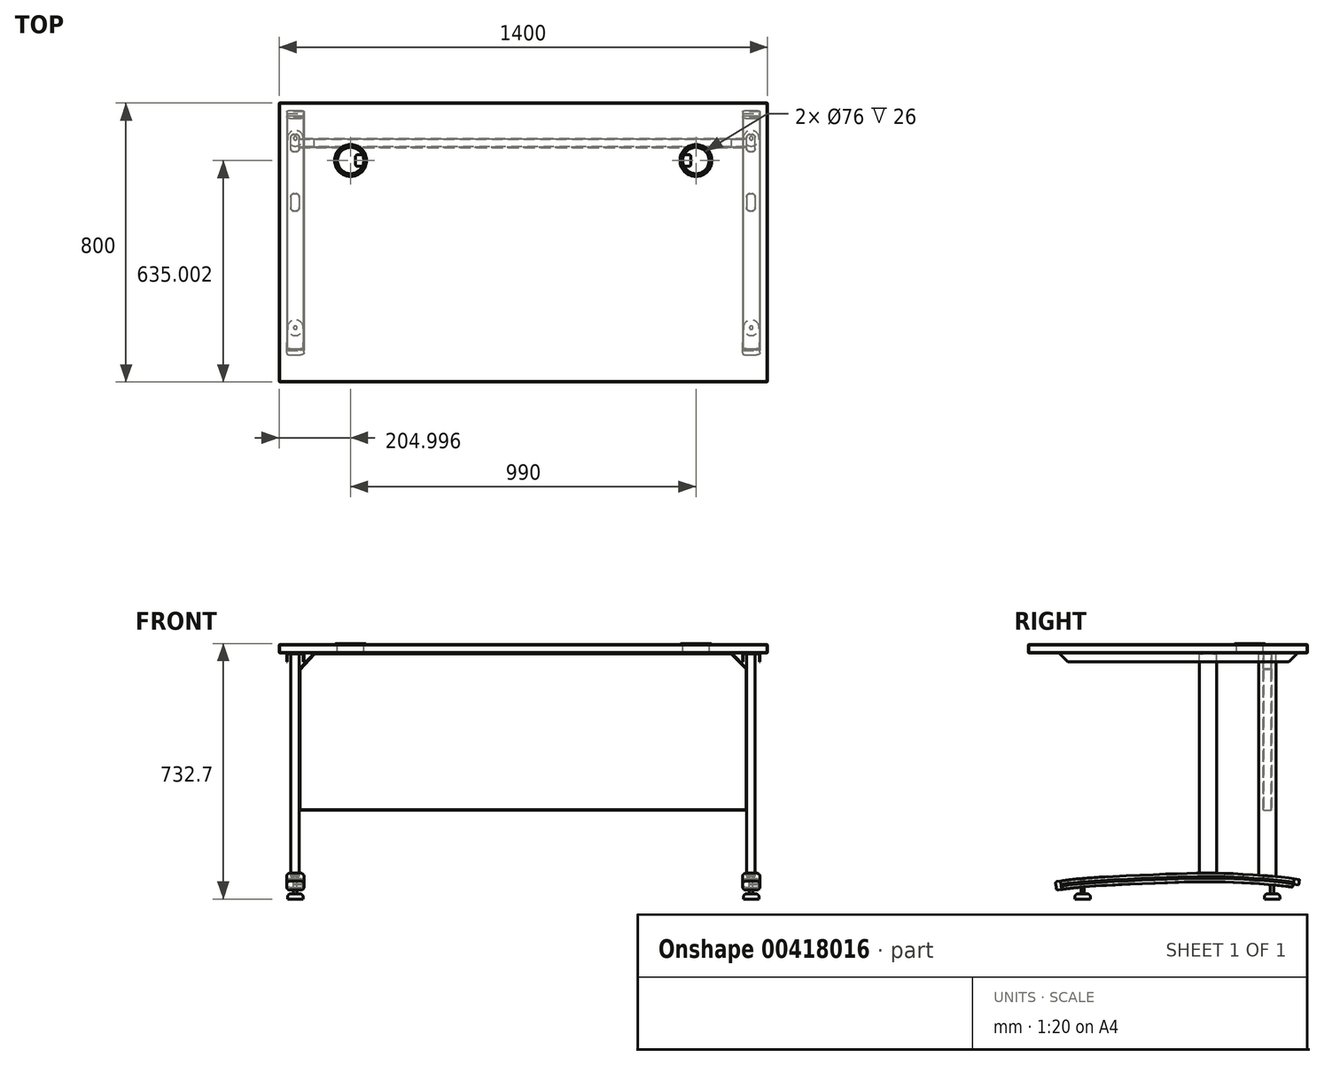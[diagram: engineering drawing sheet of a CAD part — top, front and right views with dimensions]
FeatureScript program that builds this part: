
annotation { "Feature Type Name" : "Feature", "Feature Type Description" : "" }
export const myFeature = defineFeature(function(context is Context, id is Id, definition is map)
    precondition{}
    {
        {
            var Q0;
            Q0=qCreatedBy(makeId("Top.planeOp"),FACE);
            var sketch = newSketch(context, id + "F0", { "sketchPlane" : qUnion([Q0])});
            skLineSegment(sketch, "E0.bottom", {"start": v(-639.54, 396.7) * mm, "end": v(760.46, 396.7) * mm});
            skLineSegment(sketch, "E0.top", {"start": v(-639.54, -403.3) * mm, "end": v(760.46, -403.3) * mm});
            skLineSegment(sketch, "E0.left", {"start": v(-639.54, 396.7) * mm, "end": v(-639.54, -403.3) * mm});
            skLineSegment(sketch, "E0.right", {"start": v(760.46, 396.7) * mm, "end": v(760.46, -403.3) * mm});
            skCircle(sketch, "E1", {"center": v(555.46, 231.7) * mm, "radius": 39 * mm});
            skCircle(sketch, "E2", {"center": v(-434.54, 231.7) * mm, "radius": 39 * mm});
            skSolve(sketch);
        }
        {
            var Q0;
            Q0=makeQuery(id+"F0.imprint","IMPRINT",FACE,{"disambiguationData":[TD([[makeQuery(id+"F0.imprint","IMPRINT",EDGE,{"derivedFrom":sQuery(id+"F0.wireOp",EDGE,"E0.bottom")}),-1.0]])]});
            extrude(context, id + "F1", {"entities" : qUnion([Q0]), "depth" : 25 * mm});
        }
        {
            var Q0;
            Q0=makeQuery(id+"F1.opExtrude","CAP_FACE",FACE,{"disambiguationData":[OSD([sQuery(id+"F0.wireOp",EDGE,"E0.bottom"),sQuery(id+"F0.wireOp",EDGE,"E0.top"),sQuery(id+"F0.wireOp",EDGE,"E0.left"),sQuery(id+"F0.wireOp",EDGE,"E0.right"),sQuery(id+"F0.wireOp",EDGE,"E1"),sQuery(id+"F0.wireOp",EDGE,"E2")])],"isStart":false});
            var sketch = newSketch(context, id + "F2", { "sketchPlane" : qUnion([Q0])});
            skCircle(sketch, "E3", {"center": v(555.46, 231.7) * mm, "radius": 45 * mm});
            skCircle(sketch, "E4", {"center": v(-434.54, 231.7) * mm, "radius": 45 * mm});
            skCircle(sketch, "E5", {"center": v(555.46, 231.7) * mm, "radius": 38 * mm});
            skCircle(sketch, "E6", {"center": v(555.46, 231.7) * mm, "radius": 39 * mm});
            skCircle(sketch, "E7", {"center": v(-434.54, 231.7) * mm, "radius": 39 * mm});
            skCircle(sketch, "E8", {"center": v(-434.54, 231.7) * mm, "radius": 38 * mm});
            skSolve(sketch);
        }
        {
            var Q0;
            Q0=makeQuery(id+"F2.imprint","IMPRINT",FACE,{"disambiguationData":[TD([[makeQuery(id+"F2.imprint","IMPRINT",EDGE,{"derivedFrom":sQuery(id+"F2.wireOp",EDGE,"E7")}),1.0]])]});
            var Q1;
            Q1=makeQuery(id+"F2.imprint","IMPRINT",FACE,{"disambiguationData":[TD([[makeQuery(id+"F2.imprint","IMPRINT",EDGE,{"derivedFrom":sQuery(id+"F2.wireOp",EDGE,"E5")}),-1.0]])]});
            extrude(context, id + "F3", {"entities" : qUnion([Q0, Q1]), "oppositeDirection" : true, "depth" : 25 * mm});
        }
        {
            var Q0;
            Q0=makeQuery(id+"F2.imprint","IMPRINT",FACE,{"disambiguationData":[TD([[makeQuery(id+"F2.imprint","IMPRINT",EDGE,{"derivedFrom":sQuery(id+"F2.wireOp",EDGE,"E4")}),1.0]])]});
            var Q1;
            Q1=makeQuery(id+"F2.imprint","IMPRINT",FACE,{"disambiguationData":[TD([[makeQuery(id+"F2.imprint","IMPRINT",EDGE,{"derivedFrom":sQuery(id+"F2.wireOp",EDGE,"E3")}),1.0]])]});
            var Q2;
            Q2=makeQuery(id+"F2.imprint","IMPRINT",FACE,{"disambiguationData":[TD([[makeQuery(id+"F2.imprint","IMPRINT",EDGE,{"derivedFrom":sQuery(id+"F2.wireOp",EDGE,"E7")}),1.0]])]});
            var Q3;
            Q3=makeQuery(id+"F2.imprint","IMPRINT",FACE,{"disambiguationData":[TD([[makeQuery(id+"F2.imprint","IMPRINT",EDGE,{"derivedFrom":sQuery(id+"F2.wireOp",EDGE,"E5")}),-1.0]])]});
            extrude(context, id + "F4", {"entities" : qUnion([Q0, Q1, Q2, Q3]), "operationType" : NewBodyOperationType.ADD, "depth" : 2.5 * mm});
        }
        {
            var Q0;
            Q0=makeQuery(id+"F4.opExtrude","CAP_EDGE",EDGE,{"disambiguationData":[OSD([sQuery(id+"F2.wireOp",EDGE,"E4")])],"isStart":false});
            var Q1;
            Q1=makeQuery(id+"F4.opExtrude","CAP_EDGE",EDGE,{"disambiguationData":[OSD([sQuery(id+"F2.wireOp",EDGE,"E3")])],"isStart":false});
            fillet(context, id + "F5", {"entities" : qUnion([Q0, Q1]), "radius" : 5 * mm, "tangentPropagation" : true, "allowEdgeOverflow" : false});
        }
        {
            var Q0;
            Q0=makeQuery(id+"F2.imprint","IMPRINT",FACE,{"disambiguationData":[TD([[makeQuery(id+"F2.imprint","IMPRINT",EDGE,{"derivedFrom":sQuery(id+"F2.wireOp",EDGE,"E3")}),-1.0]])]});
            var sketch = newSketch(context, id + "F6", { "sketchPlane" : qUnion([Q0])});
            skArc(sketch, "E9", {"start": v(521.32, 215.23) * mm, "mid": v(593.36, 231.7) * mm, "end": v(521.32, 248.18) * mm});
            skArc(sketch, "E10", {"start": v(-400.41, 248.18) * mm, "mid": v(-472.44, 231.7) * mm, "end": v(-400.41, 215.23) * mm});
            skLineSegment(sketch, "E11", {"start": v(521.32, 248.18) * mm, "end": v(536.1, 248.18) * mm});
            skLineSegment(sketch, "E12", {"start": v(541.1, 243.18) * mm, "end": v(541.1, 231.7) * mm});
            skLineSegment(sketch, "E13.MirrorCS", {"start": v(521.32, 215.23) * mm, "end": v(536.1, 215.23) * mm});
            skLineSegment(sketch, "E14.MirrorCS", {"start": v(541.1, 220.23) * mm, "end": v(541.1, 231.7) * mm});
            skPoint(sketch, "E15.visualSharp", {"position": v(541.1, 248.18) * mm});
            skArc(sketch, "E15.filletArc", {"start": v(541.1, 243.18) * mm, "mid": v(539.63, 246.71) * mm, "end": v(536.1, 248.18) * mm});
            skPoint(sketch, "E16.visualSharp", {"position": v(541.1, 215.23) * mm});
            skArc(sketch, "E16.filletArc", {"start": v(536.1, 215.23) * mm, "mid": v(539.63, 216.7) * mm, "end": v(541.1, 220.23) * mm});
            skLineSegment(sketch, "E17.MirrorCS", {"start": v(-400.41, 248.18) * mm, "end": v(-415.18, 248.18) * mm});
            skArc(sketch, "E18.MirrorCS", {"start": v(-420.18, 243.18) * mm, "mid": v(-418.72, 246.71) * mm, "end": v(-415.18, 248.18) * mm});
            skLineSegment(sketch, "E19.MirrorCS", {"start": v(-420.18, 243.18) * mm, "end": v(-420.18, 231.7) * mm});
            skLineSegment(sketch, "E20.MirrorCS", {"start": v(-420.18, 220.23) * mm, "end": v(-420.18, 231.7) * mm});
            skArc(sketch, "E21.MirrorCS", {"start": v(-415.18, 215.23) * mm, "mid": v(-418.72, 216.7) * mm, "end": v(-420.18, 220.23) * mm});
            skLineSegment(sketch, "E22.MirrorCS", {"start": v(-400.41, 215.23) * mm, "end": v(-415.18, 215.23) * mm});
            skSolve(sketch);
        }
        {
            var Q0;
            Q0 = qSketchRegion(id + "F6", true);
            extrude(context, id + "F7", {"entities" : qUnion([Q0]), "depth" : 2.7 * mm});
        }
        {
            var Q0;
            Q0=makeQuery(id+"F1.opExtrude","CAP_FACE",FACE,{"disambiguationData":[OSD([sQuery(id+"F0.wireOp",EDGE,"E0.bottom"),sQuery(id+"F0.wireOp",EDGE,"E0.top"),sQuery(id+"F0.wireOp",EDGE,"E0.left"),sQuery(id+"F0.wireOp",EDGE,"E0.right"),sQuery(id+"F0.wireOp",EDGE,"E1"),sQuery(id+"F0.wireOp",EDGE,"E2")])],"isStart":false});
            var Q1;
            Q1=makeQuery(id+"F1.opExtrude","CAP_FACE",FACE,{"disambiguationData":[OSD([sQuery(id+"F0.wireOp",EDGE,"E0.bottom"),sQuery(id+"F0.wireOp",EDGE,"E0.top"),sQuery(id+"F0.wireOp",EDGE,"E0.left"),sQuery(id+"F0.wireOp",EDGE,"E0.right"),sQuery(id+"F0.wireOp",EDGE,"E1"),sQuery(id+"F0.wireOp",EDGE,"E2")])],"isStart":true});
            var Q2;
            Q2=makeQuery(id+"F1.opExtrude","SWEPT_EDGE",EDGE,{"disambiguationData":[OSD([sQuery(id+"F0.wireOp",EDGE,"E0.top"),sQuery(id+"F0.wireOp",EDGE,"E0.right")])]});
            var Q3;
            Q3=makeQuery(id+"F1.opExtrude","SWEPT_EDGE",EDGE,{"disambiguationData":[OSD([sQuery(id+"F0.wireOp",EDGE,"E0.bottom"),sQuery(id+"F0.wireOp",EDGE,"E0.right")])]});
            var Q4;
            Q4=makeQuery(id+"F1.opExtrude","SWEPT_EDGE",EDGE,{"disambiguationData":[OSD([sQuery(id+"F0.wireOp",EDGE,"E0.bottom"),sQuery(id+"F0.wireOp",EDGE,"E0.left")])]});
            var Q5;
            Q5=makeQuery(id+"F1.opExtrude","SWEPT_EDGE",EDGE,{"disambiguationData":[OSD([sQuery(id+"F0.wireOp",EDGE,"E0.top"),sQuery(id+"F0.wireOp",EDGE,"E0.left")])]});
            chamfer(context, id + "F8", {"entities" : qUnion([Q0, Q1, Q2, Q3, Q4, Q5]), "width" : 1.5 * mm, "tangentPropagation" : true});
        }
        {
            var Q0;
            Q0=makeQuery(id+"F1.opExtrude","SWEPT_FACE",FACE,{"disambiguationData":[OSD([sQuery(id+"F0.wireOp",EDGE,"E0.top")])]});
            var sketch = newSketch(context, id + "F9", { "sketchPlane" : qUnion([Q0])});
            skLineSegment(sketch, "E23.bottom", {"start": v(708.96, 0) * mm, "end": v(758.96, 0) * mm});
            skLineSegment(sketch, "E23.top", {"start": v(708.96, -25) * mm, "end": v(710.96, -25) * mm});
            skLineSegment(sketch, "E23.left", {"start": v(708.96, 0) * mm, "end": v(708.96, -25) * mm});
            skLineSegment(sketch, "E23.right", {"start": v(758.96, 0) * mm, "end": v(758.96, -25) * mm});
            skLineSegment(sketch, "E24.0", {"start": v(756.96, -2) * mm, "end": v(756.96, -25) * mm});
            skLineSegment(sketch, "E24.1", {"start": v(710.96, -2) * mm, "end": v(756.96, -2) * mm});
            skLineSegment(sketch, "E24.2", {"start": v(710.96, -2) * mm, "end": v(710.96, -25) * mm});
            skLineSegment(sketch, "E25.trimOffspring", {"start": v(756.96, -25) * mm, "end": v(758.96, -25) * mm});
            skLineSegment(sketch, "E26", {"start": v(60.46, 1.5) * mm, "end": v(60.46, 145.21) * mm});
            skPoint(sketch, "E26.endSnap0", {"position": v(60.46, 23.5) * mm});
            skLineSegment(sketch, "E27.MirrorCS", {"start": v(-588.04, 0) * mm, "end": v(-638.04, 0) * mm});
            skLineSegment(sketch, "E28.MirrorCS", {"start": v(-590.04, -2) * mm, "end": v(-636.04, -2) * mm});
            skLineSegment(sketch, "E29.MirrorCS", {"start": v(-588.04, 0) * mm, "end": v(-588.04, -25) * mm});
            skLineSegment(sketch, "E30.MirrorCS", {"start": v(-590.04, -2) * mm, "end": v(-590.04, -25) * mm});
            skLineSegment(sketch, "E31.MirrorCS", {"start": v(-636.04, -2) * mm, "end": v(-636.04, -25) * mm});
            skLineSegment(sketch, "E32.MirrorCS", {"start": v(-638.04, 0) * mm, "end": v(-638.04, -25) * mm});
            skLineSegment(sketch, "E33.MirrorCS", {"start": v(-636.04, -25) * mm, "end": v(-638.04, -25) * mm});
            skLineSegment(sketch, "E34.MirrorCS", {"start": v(-588.04, -25) * mm, "end": v(-590.04, -25) * mm});
            skSolve(sketch);
        }
        {
            var Q0;
            Q0 = qSketchRegion(id + "F9", true);
            extrude(context, id + "F10", {"entities" : qUnion([Q0]), "oppositeDirection" : true, "depth" : 680 * mm});
        }
        {
            var Q0;
            Q0=makeQuery(id+"F10.opExtrude","CAP_EDGE",EDGE,{"disambiguationData":[OSD([sQuery(id+"F9.wireOp",EDGE,"E25.trimOffspring")])],"isStart":true});
            var Q1;
            Q1=makeQuery(id+"F10.opExtrude","CAP_EDGE",EDGE,{"disambiguationData":[OSD([sQuery(id+"F9.wireOp",EDGE,"E23.top")])],"isStart":true});
            var Q2;
            Q2=makeQuery(id+"F10.opExtrude","CAP_EDGE",EDGE,{"disambiguationData":[OSD([sQuery(id+"F9.wireOp",EDGE,"E33.MirrorCS")])],"isStart":true});
            var Q3;
            Q3=makeQuery(id+"F10.opExtrude","CAP_EDGE",EDGE,{"disambiguationData":[OSD([sQuery(id+"F9.wireOp",EDGE,"E34.MirrorCS")])],"isStart":true});
            var Q4;
            Q4=makeQuery(id+"F10.opExtrude","CAP_EDGE",EDGE,{"disambiguationData":[OSD([sQuery(id+"F9.wireOp",EDGE,"E33.MirrorCS")])],"isStart":false});
            var Q5;
            Q5=makeQuery(id+"F10.opExtrude","CAP_EDGE",EDGE,{"disambiguationData":[OSD([sQuery(id+"F9.wireOp",EDGE,"E34.MirrorCS")])],"isStart":false});
            var Q6;
            Q6=makeQuery(id+"F10.opExtrude","CAP_EDGE",EDGE,{"disambiguationData":[OSD([sQuery(id+"F9.wireOp",EDGE,"E25.trimOffspring")])],"isStart":false});
            var Q7;
            Q7=makeQuery(id+"F10.opExtrude","CAP_EDGE",EDGE,{"disambiguationData":[OSD([sQuery(id+"F9.wireOp",EDGE,"E23.top")])],"isStart":false});
            chamfer(context, id + "F11", {"entities" : qUnion([Q0, Q1, Q2, Q3, Q4, Q5, Q6, Q7]), "width" : 23 * mm, "tangentPropagation" : true});
        }
        {
            var Q0;
            Q0=makeQuery(id+"F1.opExtrude","SWEPT_FACE",FACE,{"disambiguationData":[OSD([sQuery(id+"F0.wireOp",EDGE,"E0.top")])]});
            var sketch = newSketch(context, id + "F12", { "sketchPlane" : qUnion([Q0])});
            skLineSegment(sketch, "E35.bottom", {"start": v(718.96, -42.04) * mm, "end": v(748.96, -42.04) * mm});
            skLineSegment(sketch, "E35.top", {"start": v(718.96, -67.04) * mm, "end": v(748.96, -67.04) * mm});
            skLineSegment(sketch, "E35.left", {"start": v(708.96, -52.04) * mm, "end": v(708.96, -57.04) * mm});
            skLineSegment(sketch, "E35.right", {"start": v(758.96, -52.04) * mm, "end": v(758.96, -57.04) * mm});
            skPoint(sketch, "E36.visualSharp", {"position": v(708.96, -42.04) * mm});
            skArc(sketch, "E36.filletArc", {"start": v(718.96, -42.04) * mm, "mid": v(711.88, -44.97) * mm, "end": v(708.96, -52.04) * mm});
            skPoint(sketch, "E37.visualSharp", {"position": v(758.96, -42.04) * mm});
            skArc(sketch, "E37.filletArc", {"start": v(758.96, -52.04) * mm, "mid": v(756.03, -44.97) * mm, "end": v(748.96, -42.04) * mm});
            skPoint(sketch, "E38.visualSharp", {"position": v(758.96, -67.04) * mm});
            skArc(sketch, "E38.filletArc", {"start": v(748.96, -67.04) * mm, "mid": v(756.03, -64.1) * mm, "end": v(758.96, -57.04) * mm});
            skPoint(sketch, "E39.visualSharp", {"position": v(708.96, -67.04) * mm});
            skArc(sketch, "E39.filletArc", {"start": v(708.96, -57.04) * mm, "mid": v(711.88, -64.1) * mm, "end": v(718.96, -67.04) * mm});
            skSolve(sketch);
        }
        {
            var Q0;
            Q0=makeQuery(id+"F1.opExtrude","SWEPT_FACE",FACE,{"disambiguationData":[OSD([sQuery(id+"F0.wireOp",EDGE,"E0.right")])]});
            var sketch = newSketch(context, id + "F13", { "sketchPlane" : qUnion([Q0])});
            skFitSpline(sketch, "E40", {"points": [v(-405.93, -54.71) * mm, v(-106.77, -33.77) * mm, v(108.63, -32.91) * mm, v(268.36, -47.14) * mm], "startDerivative": vector(317.93, 78.58) * mm, "endDerivative": vector(232.96, -46.8) * mm});
            skSolve(sketch);
        }
        {
            var Q0;
            Q0=makeQuery(id+"F12.imprint","IMPRINT",FACE,{"disambiguationData":[TD([[makeQuery(id+"F12.imprint","IMPRINT",EDGE,{"derivedFrom":sQuery(id+"F12.wireOp",EDGE,"E35.bottom")}),-1.0]])]});
            var Q1;
            Q1=sQuery(id+"F13.wireOp",EDGE,"E40");
            sweep(context, id + "F14", {"profiles" : qUnion([Q0]), "path" : qUnion([Q1])});
        }
        {
            var Q0;
            Q0=makeQuery(id+"F14.opSweep","SWEPT_FACE",FACE,{"disambiguationData":[OSD([sQuery(id+"F12.wireOp",EDGE,"E35.right"),sQuery(id+"F13.wireOp",EDGE,"E40")])]});
            var sketch = newSketch(context, id + "F15", { "sketchPlane" : qUnion([Q0])});
            skLineSegment(sketch, "E41", {"start": v(263.84, -72.6) * mm, "end": v(270.82, -20.08) * mm});
            skPoint(sketch, "E41.endSnap0", {"position": v(270.82, -48.1) * mm});
            skLineSegment(sketch, "E42", {"start": v(270.82, -20.08) * mm, "end": v(310.84, -39.43) * mm});
            skLineSegment(sketch, "E43", {"start": v(310.84, -39.43) * mm, "end": v(287, -77.1) * mm});
            skLineSegment(sketch, "E44", {"start": v(263.84, -72.6) * mm, "end": v(287, -77.1) * mm});
            skLineSegment(sketch, "E45", {"start": v(-403.3, -25.95) * mm, "end": v(-393.36, -96.44) * mm});
            skLineSegment(sketch, "E46", {"start": v(-403.3, -25.95) * mm, "end": v(-431.37, -45.85) * mm});
            skLineSegment(sketch, "E47", {"start": v(-431.37, -45.85) * mm, "end": v(-408.22, -99.55) * mm});
            skLineSegment(sketch, "E48", {"start": v(-393.36, -96.44) * mm, "end": v(-408.22, -99.55) * mm});
            skSolve(sketch);
        }
        {
            var Q0;
            Q0 = qSketchRegion(id + "F15", true);
            extrude(context, id + "F16", {"entities" : qUnion([Q0]), "operationType" : NewBodyOperationType.REMOVE, "oppositeDirection" : true, "depth" : 60 * mm});
        }
        {
            var Q0;
            Q0=makeQuery(id+"F16.boolean.opBoolean","COPY",FACE,{"derivedFrom":makeQuery(id+"F16.opExtrude","SWEPT_FACE",FACE,{"disambiguationData":[OSD([sQuery(id+"F15.wireOp",EDGE,"E45")])]})});
            extrude(context, id + "F17", {"entities" : qUnion([Q0]), "depth" : 15 * mm});
        }
        {
            var Q0;
            Q0=makeQuery(id+"F16.boolean.opBoolean","COPY",FACE,{"derivedFrom":makeQuery(id+"F16.opExtrude","SWEPT_FACE",FACE,{"disambiguationData":[OSD([sQuery(id+"F15.wireOp",EDGE,"E41")])]})});
            extrude(context, id + "F18", {"entities" : qUnion([Q0]), "depth" : 15 * mm});
        }
        {
            var Q0;
            Q0=makeQuery(id+"F17.opExtrude","CAP_FACE",FACE,{"disambiguationData":[OSD([sQuery(id+"F15.wireOp",EDGE,"E45")])],"isStart":false});
            var Q1;
            Q1=makeQuery(id+"F18.opExtrude","CAP_FACE",FACE,{"disambiguationData":[OSD([sQuery(id+"F15.wireOp",EDGE,"E41")])],"isStart":false});
            fillet(context, id + "F19", {"entities" : qUnion([Q0, Q1]), "radius" : 5 * mm, "tangentPropagation" : true, "allowEdgeOverflow" : false});
        }
        {
            var Q0;
            Q0=makeQuery(id+"F10.opExtrude","SWEPT_FACE",FACE,{"disambiguationData":[OSD([sQuery(id+"F9.wireOp",EDGE,"E24.1")])]});
            var sketch = newSketch(context, id + "F20", { "sketchPlane" : qUnion([Q0])});
            skCircle(sketch, "E49", {"center": v(733.96, 337.68) * mm, "radius": 5 * mm});
            skPoint(sketch, "E49.centerSnap0", {"position": v(733.96, 403.3) * mm});
            skCircle(sketch, "E50", {"center": v(733.96, -205.49) * mm, "radius": 5 * mm});
            skPoint(sketch, "E50.centerSnap0", {"position": v(733.96, -276.7) * mm});
            skSolve(sketch);
        }
        {
            var Q0;
            Q0 = qSketchRegion(id + "F20", true);
            extrude(context, id + "F21", {"entities" : qUnion([Q0]), "depth" : 80 * mm, "hasSecondDirection" : true, "secondDirectionOppositeDirection" : true, "secondDirectionDepth" : -40 * mm});
        }
        {
            var Q0;
            Q0=makeQuery(id+"F21.opExtrude","CAP_FACE",FACE,{"disambiguationData":[OSD([sQuery(id+"F20.wireOp",EDGE,"E50")])],"isStart":false});
            var sketch = newSketch(context, id + "F22", { "sketchPlane" : qUnion([Q0])});
            skCircle(sketch, "E51", {"center": v(733.96, -205.49) * mm, "radius": 22.5 * mm});
            skCircle(sketch, "E52", {"center": v(733.97, 337.74) * mm, "radius": 22.5 * mm});
            skSolve(sketch);
        }
        {
            var Q0;
            Q0 = qSketchRegion(id + "F22", true);
            extrude(context, id + "F23", {"entities" : qUnion([Q0]), "depth" : 15 * mm});
        }
        {
            var Q0;
            Q0=makeQuery(id+"F23.opExtrude","CAP_EDGE",EDGE,{"disambiguationData":[OSD([sQuery(id+"F22.wireOp",EDGE,"E52")])],"isStart":true});
            var Q1;
            Q1=makeQuery(id+"F23.opExtrude","CAP_EDGE",EDGE,{"disambiguationData":[OSD([sQuery(id+"F22.wireOp",EDGE,"E51")])],"isStart":true});
            fillet(context, id + "F24", {"entities" : qUnion([Q0, Q1]), "radius" : 10 * mm, "tangentPropagation" : true, "allowEdgeOverflow" : false});
        }
        {
            var Q0;
            Q0=makeQuery(id+"F21.opExtrude","SWEPT_BODY",BODY,{"disambiguationData":[OSD([sQuery(id+"F20.wireOp",EDGE,"E49")])]});
            var Q1;
            Q1=makeQuery(id+"F23.opExtrude","SWEPT_BODY",BODY,{"disambiguationData":[OSD([sQuery(id+"F22.wireOp",EDGE,"E52")])]});
            var Q2;
            Q2=makeQuery(id+"F21.opExtrude","SWEPT_BODY",BODY,{"disambiguationData":[OSD([sQuery(id+"F20.wireOp",EDGE,"E50")])]});
            var Q3;
            Q3=makeQuery(id+"F23.opExtrude","SWEPT_BODY",BODY,{"disambiguationData":[OSD([sQuery(id+"F22.wireOp",EDGE,"E51")])]});
            transform(context, id + "F25", {"entities" : qUnion([Q0, Q1, Q2, Q3]), "transformType" : TransformType.TRANSLATION_3D, "dx" : 0 * mm, "dy" : 0 * mm, "dz" : 4 * mm, "makeCopy" : false});
        }
        {
            var Q0;
            Q0=makeQuery(id+"F17.opExtrude","SWEPT_BODY",BODY,{"disambiguationData":[OSD([sQuery(id+"F15.wireOp",EDGE,"E45")])]});
            var Q1;
            Q1=makeQuery(id+"F14.opSweep","SWEPT_BODY",BODY,{"disambiguationData":[OSD([sQuery(id+"F12.wireOp",EDGE,"E35.bottom"),sQuery(id+"F12.wireOp",EDGE,"E35.top"),sQuery(id+"F12.wireOp",EDGE,"E35.left"),sQuery(id+"F12.wireOp",EDGE,"E35.right"),sQuery(id+"F12.wireOp",EDGE,"E36.filletArc"),sQuery(id+"F12.wireOp",EDGE,"E37.filletArc"),sQuery(id+"F12.wireOp",EDGE,"E38.filletArc"),sQuery(id+"F12.wireOp",EDGE,"E39.filletArc"),sQuery(id+"F13.wireOp",EDGE,"E40")])]});
            var Q2;
            Q2=makeQuery(id+"F21.opExtrude","SWEPT_BODY",BODY,{"disambiguationData":[OSD([sQuery(id+"F20.wireOp",EDGE,"E49")])]});
            var Q3;
            Q3=makeQuery(id+"F23.opExtrude","SWEPT_BODY",BODY,{"disambiguationData":[OSD([sQuery(id+"F22.wireOp",EDGE,"E52")])]});
            var Q4;
            Q4=makeQuery(id+"F18.opExtrude","SWEPT_BODY",BODY,{"disambiguationData":[OSD([sQuery(id+"F15.wireOp",EDGE,"E41")])]});
            var Q5;
            Q5=makeQuery(id+"F21.opExtrude","SWEPT_BODY",BODY,{"disambiguationData":[OSD([sQuery(id+"F20.wireOp",EDGE,"E50")])]});
            var Q6;
            Q6=makeQuery(id+"F23.opExtrude","SWEPT_BODY",BODY,{"disambiguationData":[OSD([sQuery(id+"F22.wireOp",EDGE,"E51")])]});
            transform(context, id + "F26", {"entities" : qUnion([Q0, Q1, Q2, Q3, Q4, Q5, Q6]), "transformType" : TransformType.TRANSLATION_3D, "dx" : 0 * mm, "dy" : 0 * mm, "dz" : -700 * mm, "makeCopy" : false});
        }
        {
            var Q0;
            Q0=makeQuery(id+"F17.opExtrude","SWEPT_BODY",BODY,{"disambiguationData":[OSD([sQuery(id+"F15.wireOp",EDGE,"E45")])]});
            var Q1;
            Q1=makeQuery(id+"F14.opSweep","SWEPT_BODY",BODY,{"disambiguationData":[OSD([sQuery(id+"F12.wireOp",EDGE,"E35.bottom"),sQuery(id+"F12.wireOp",EDGE,"E35.top"),sQuery(id+"F12.wireOp",EDGE,"E35.left"),sQuery(id+"F12.wireOp",EDGE,"E35.right"),sQuery(id+"F12.wireOp",EDGE,"E36.filletArc"),sQuery(id+"F12.wireOp",EDGE,"E37.filletArc"),sQuery(id+"F12.wireOp",EDGE,"E38.filletArc"),sQuery(id+"F12.wireOp",EDGE,"E39.filletArc"),sQuery(id+"F13.wireOp",EDGE,"E40")])]});
            var Q2;
            Q2=makeQuery(id+"F21.opExtrude","SWEPT_BODY",BODY,{"disambiguationData":[OSD([sQuery(id+"F20.wireOp",EDGE,"E49")])]});
            var Q3;
            Q3=makeQuery(id+"F23.opExtrude","SWEPT_BODY",BODY,{"disambiguationData":[OSD([sQuery(id+"F22.wireOp",EDGE,"E52")])]});
            var Q4;
            Q4=makeQuery(id+"F18.opExtrude","SWEPT_BODY",BODY,{"disambiguationData":[OSD([sQuery(id+"F15.wireOp",EDGE,"E41")])]});
            var Q5;
            Q5=makeQuery(id+"F21.opExtrude","SWEPT_BODY",BODY,{"disambiguationData":[OSD([sQuery(id+"F20.wireOp",EDGE,"E50")])]});
            var Q6;
            Q6=makeQuery(id+"F23.opExtrude","SWEPT_BODY",BODY,{"disambiguationData":[OSD([sQuery(id+"F22.wireOp",EDGE,"E51")])]});
            transform(context, id + "F27", {"entities" : qUnion([Q0, Q1, Q2, Q3, Q4, Q5, Q6]), "transformType" : TransformType.TRANSLATION_3D, "dx" : 0 * mm, "dy" : 0 * mm, "dz" : 88 * mm, "makeCopy" : false});
        }
        {
            var Q0;
            Q0=makeQuery(id+"F10.opExtrude","SWEPT_BODY",BODY,{"disambiguationData":[OSD([sQuery(id+"F9.wireOp",EDGE,"E23.bottom"),sQuery(id+"F9.wireOp",EDGE,"E23.top"),sQuery(id+"F9.wireOp",EDGE,"E23.left"),sQuery(id+"F9.wireOp",EDGE,"E23.right"),sQuery(id+"F9.wireOp",EDGE,"E24.0"),sQuery(id+"F9.wireOp",EDGE,"E24.1"),sQuery(id+"F9.wireOp",EDGE,"E24.2"),sQuery(id+"F9.wireOp",EDGE,"E25.trimOffspring")])]});
            var Q1;
            Q1=makeQuery(id+"F18.opExtrude","SWEPT_BODY",BODY,{"disambiguationData":[OSD([sQuery(id+"F15.wireOp",EDGE,"E41")])]});
            var Q2;
            Q2=makeQuery(id+"F23.opExtrude","SWEPT_BODY",BODY,{"disambiguationData":[OSD([sQuery(id+"F22.wireOp",EDGE,"E52")])]});
            var Q3;
            Q3=makeQuery(id+"F14.opSweep","SWEPT_BODY",BODY,{"disambiguationData":[OSD([sQuery(id+"F12.wireOp",EDGE,"E35.bottom"),sQuery(id+"F12.wireOp",EDGE,"E35.top"),sQuery(id+"F12.wireOp",EDGE,"E35.left"),sQuery(id+"F12.wireOp",EDGE,"E35.right"),sQuery(id+"F12.wireOp",EDGE,"E36.filletArc"),sQuery(id+"F12.wireOp",EDGE,"E37.filletArc"),sQuery(id+"F12.wireOp",EDGE,"E38.filletArc"),sQuery(id+"F12.wireOp",EDGE,"E39.filletArc"),sQuery(id+"F13.wireOp",EDGE,"E40")])]});
            var Q4;
            Q4=makeQuery(id+"F17.opExtrude","SWEPT_BODY",BODY,{"disambiguationData":[OSD([sQuery(id+"F15.wireOp",EDGE,"E45")])]});
            var Q5;
            Q5=makeQuery(id+"F21.opExtrude","SWEPT_BODY",BODY,{"disambiguationData":[OSD([sQuery(id+"F20.wireOp",EDGE,"E49")])]});
            var Q6;
            Q6=makeQuery(id+"F21.opExtrude","SWEPT_BODY",BODY,{"disambiguationData":[OSD([sQuery(id+"F20.wireOp",EDGE,"E50")])]});
            var Q7;
            Q7=makeQuery(id+"F23.opExtrude","SWEPT_BODY",BODY,{"disambiguationData":[OSD([sQuery(id+"F22.wireOp",EDGE,"E51")])]});
            transform(context, id + "F28", {"entities" : qUnion([Q0, Q1, Q2, Q3, Q4, Q5, Q6, Q7]), "transformType" : TransformType.TRANSLATION_3D, "dx" : -20 * mm, "dy" : 90 * mm, "dz" : 0 * mm, "makeCopy" : false});
        }
        {
            var Q0;
            Q0=makeQuery(id+"F10.opExtrude","SWEPT_BODY",BODY,{"disambiguationData":[OSD([sQuery(id+"F9.wireOp",EDGE,"E27.MirrorCS"),sQuery(id+"F9.wireOp",EDGE,"E28.MirrorCS"),sQuery(id+"F9.wireOp",EDGE,"E29.MirrorCS"),sQuery(id+"F9.wireOp",EDGE,"E30.MirrorCS"),sQuery(id+"F9.wireOp",EDGE,"E31.MirrorCS"),sQuery(id+"F9.wireOp",EDGE,"E32.MirrorCS"),sQuery(id+"F9.wireOp",EDGE,"E33.MirrorCS"),sQuery(id+"F9.wireOp",EDGE,"E34.MirrorCS")])]});
            deleteBodies(context, id + "F29", {"entities" : qUnion([Q0])});
        }
        {
            var Q0;
            Q0=makeQuery(id+"F10.opExtrude","SWEPT_FACE",FACE,{"disambiguationData":[OSD([sQuery(id+"F9.wireOp",EDGE,"E24.1")])]});
            var sketch = newSketch(context, id + "F30", { "sketchPlane" : qUnion([Q0])});
            skLineSegment(sketch, "E53.bottom", {"start": v(710.46, -256.7) * mm, "end": v(715.46, -256.7) * mm});
            skLineSegment(sketch, "E53.top", {"start": v(710.46, -306.7) * mm, "end": v(715.46, -306.7) * mm});
            skLineSegment(sketch, "E53.left", {"start": v(700.46, -266.7) * mm, "end": v(700.46, -296.7) * mm});
            skLineSegment(sketch, "E53.right", {"start": v(725.46, -266.7) * mm, "end": v(725.46, -296.7) * mm});
            skPoint(sketch, "E54.visualSharp", {"position": v(700.46, -256.7) * mm});
            skArc(sketch, "E54.filletArc", {"start": v(710.46, -256.7) * mm, "mid": v(703.38, -259.63) * mm, "end": v(700.46, -266.7) * mm});
            skPoint(sketch, "E55.visualSharp", {"position": v(725.46, -256.7) * mm});
            skArc(sketch, "E55.filletArc", {"start": v(725.46, -266.7) * mm, "mid": v(722.53, -259.63) * mm, "end": v(715.46, -256.7) * mm});
            skPoint(sketch, "E56.visualSharp", {"position": v(725.46, -306.7) * mm});
            skArc(sketch, "E56.filletArc", {"start": v(715.46, -306.7) * mm, "mid": v(722.53, -303.77) * mm, "end": v(725.46, -296.7) * mm});
            skPoint(sketch, "E57.visualSharp", {"position": v(700.46, -306.7) * mm});
            skArc(sketch, "E57.filletArc", {"start": v(700.46, -296.7) * mm, "mid": v(703.38, -303.77) * mm, "end": v(710.46, -306.7) * mm});
            skLineSegment(sketch, "E58.MirrorCS", {"start": v(700.46, -126.7) * mm, "end": v(700.46, -96.7) * mm});
            skLineSegment(sketch, "E59.MirrorCS", {"start": v(725.46, -126.7) * mm, "end": v(725.46, -96.7) * mm});
            skArc(sketch, "E60.MirrorCS", {"start": v(710.46, -136.7) * mm, "mid": v(703.38, -133.77) * mm, "end": v(700.46, -126.7) * mm});
            skArc(sketch, "E61.MirrorCS", {"start": v(725.46, -126.7) * mm, "mid": v(722.53, -133.77) * mm, "end": v(715.46, -136.7) * mm});
            skLineSegment(sketch, "E62.MirrorCS", {"start": v(710.46, -136.7) * mm, "end": v(715.46, -136.7) * mm});
            skArc(sketch, "E63.MirrorCS", {"start": v(700.46, -96.7) * mm, "mid": v(703.38, -89.63) * mm, "end": v(710.46, -86.7) * mm});
            skArc(sketch, "E64.MirrorCS", {"start": v(715.46, -86.7) * mm, "mid": v(722.53, -89.63) * mm, "end": v(725.46, -96.7) * mm});
            skLineSegment(sketch, "E65.MirrorCS", {"start": v(710.46, -86.7) * mm, "end": v(715.46, -86.7) * mm});
            skSolve(sketch);
        }
        {
            var Q0;
            Q0 = qSketchRegion(id + "F30", true);
            extrude(context, id + "F31", {"entities" : qUnion([Q0]), "operationType" : NewBodyOperationType.ADD, "depth" : 652 * mm});
        }
        {
            var Q0;
            Q0=makeQuery(id+"F10.opExtrude","SWEPT_BODY",BODY,{"disambiguationData":[OSD([sQuery(id+"F9.wireOp",EDGE,"E23.bottom"),sQuery(id+"F9.wireOp",EDGE,"E23.top"),sQuery(id+"F9.wireOp",EDGE,"E23.left"),sQuery(id+"F9.wireOp",EDGE,"E23.right"),sQuery(id+"F9.wireOp",EDGE,"E24.0"),sQuery(id+"F9.wireOp",EDGE,"E24.1"),sQuery(id+"F9.wireOp",EDGE,"E24.2"),sQuery(id+"F9.wireOp",EDGE,"E25.trimOffspring")])]});
            var Q1;
            Q1=makeQuery(id+"F23.opExtrude","SWEPT_BODY",BODY,{"disambiguationData":[OSD([sQuery(id+"F22.wireOp",EDGE,"E52")])]});
            var Q2;
            Q2=makeQuery(id+"F14.opSweep","SWEPT_BODY",BODY,{"disambiguationData":[OSD([sQuery(id+"F12.wireOp",EDGE,"E35.bottom"),sQuery(id+"F12.wireOp",EDGE,"E35.top"),sQuery(id+"F12.wireOp",EDGE,"E35.left"),sQuery(id+"F12.wireOp",EDGE,"E35.right"),sQuery(id+"F12.wireOp",EDGE,"E36.filletArc"),sQuery(id+"F12.wireOp",EDGE,"E37.filletArc"),sQuery(id+"F12.wireOp",EDGE,"E38.filletArc"),sQuery(id+"F12.wireOp",EDGE,"E39.filletArc"),sQuery(id+"F13.wireOp",EDGE,"E40")])]});
            var Q3;
            Q3=makeQuery(id+"F17.opExtrude","SWEPT_BODY",BODY,{"disambiguationData":[OSD([sQuery(id+"F15.wireOp",EDGE,"E45")])]});
            var Q4;
            Q4=makeQuery(id+"F23.opExtrude","SWEPT_BODY",BODY,{"disambiguationData":[OSD([sQuery(id+"F22.wireOp",EDGE,"E51")])]});
            var Q5;
            Q5=makeQuery(id+"F21.opExtrude","SWEPT_BODY",BODY,{"disambiguationData":[OSD([sQuery(id+"F20.wireOp",EDGE,"E50")])]});
            var Q6;
            Q6=makeQuery(id+"F18.opExtrude","SWEPT_BODY",BODY,{"disambiguationData":[OSD([sQuery(id+"F15.wireOp",EDGE,"E41")])]});
            var Q7;
            Q7=makeQuery(id+"F21.opExtrude","SWEPT_BODY",BODY,{"disambiguationData":[OSD([sQuery(id+"F20.wireOp",EDGE,"E49")])]});
            transform(context, id + "F32", {"entities" : qUnion([Q0, Q1, Q2, Q3, Q4, Q5, Q6, Q7]), "transformType" : TransformType.TRANSLATION_3D, "dx" : -1307 * mm, "dy" : 0 * mm, "dz" : 0 * mm, "makeCopy" : true});
        }
        {
            var Q0;
            Q0=makeQuery(id+"F31.opExtrude","SWEPT_FACE",FACE,{"disambiguationData":[OSD([sQuery(id+"F30.wireOp",EDGE,"E53.top")])]});
            var sketch = newSketch(context, id + "F33", { "sketchPlane" : qUnion([Q0])});
            skLineSegment(sketch, "E66.bottom", {"start": v(-657.2, 0) * mm, "end": v(538.3, 0) * mm});
            skLineSegment(sketch, "E66.top", {"start": v(-700.46, -450) * mm, "end": v(581.54, -450) * mm});
            skLineSegment(sketch, "E66.left", {"start": v(-700.46, -44.23) * mm, "end": v(-700.46, -450) * mm});
            skLineSegment(sketch, "E66.right", {"start": v(581.54, -46.45) * mm, "end": v(581.54, -450) * mm});
            skLineSegment(sketch, "E67", {"start": v(-700.46, -44.23) * mm, "end": v(-657.2, 0) * mm});
            skLineSegment(sketch, "E68.MirrorCS", {"start": v(581.54, -46.45) * mm, "end": v(538.3, 0) * mm});
            skSolve(sketch);
        }
        {
            var Q0;
            Q0=makeQuery(id+"F33.imprint","IMPRINT",FACE,{"disambiguationData":[TD([[makeQuery(id+"F33.imprint","IMPRINT",EDGE,{"derivedFrom":sQuery(id+"F33.wireOp",EDGE,"E66.bottom")}),-1.0]])]});
            extrude(context, id + "F34", {"entities" : qUnion([Q0]), "oppositeDirection" : true, "depth" : (50 - 12.5) * mm, "hasSecondDirection" : true, "secondDirectionOppositeDirection" : false, "secondDirectionDepth" : -12.5 * mm});
        }
        {
            var Q0;
            Q0=makeQuery(id+"F34.opExtrude","CAP_FACE",FACE,{"disambiguationData":[OSD([sQuery(id+"F33.wireOp",EDGE,"E66.bottom"),sQuery(id+"F33.wireOp",EDGE,"E66.top"),sQuery(id+"F33.wireOp",EDGE,"E66.left"),sQuery(id+"F33.wireOp",EDGE,"E66.right"),sQuery(id+"F33.wireOp",EDGE,"E67"),sQuery(id+"F33.wireOp",EDGE,"E68.MirrorCS")])],"isStart":true});
            var Q1;
            Q1=makeQuery(id+"F34.opExtrude","CAP_FACE",FACE,{"disambiguationData":[OSD([sQuery(id+"F33.wireOp",EDGE,"E66.bottom"),sQuery(id+"F33.wireOp",EDGE,"E66.top"),sQuery(id+"F33.wireOp",EDGE,"E66.left"),sQuery(id+"F33.wireOp",EDGE,"E66.right"),sQuery(id+"F33.wireOp",EDGE,"E67"),sQuery(id+"F33.wireOp",EDGE,"E68.MirrorCS")])],"isStart":false});
            chamfer(context, id + "F35", {"entities" : qUnion([Q0, Q1]), "width" : 1.5 * mm, "tangentPropagation" : true});
        }
    });
